# Revit family: RN 90044 Optifitt-Serra-Nippel doppio
name_source: partatom
category: Rohrformteile
units: mm (PartAtom-declared; Revit-internal decimal feet)

## family parameters
Arbeitsebenenbasiert = Nein
Beim Laden mit Abzugskörper schneiden = Nein
Bemaßung runder Anschluss = Durchmesser verwenden
Gemeinsam genutzt = Nein
Immer vertikal = Ja
Teiletyp = Nicht definiert

## types (5) — shared parameters
1.010.00.2 Blattnummer der Richtlinie = 29
1.010.00.3 Ausgabedatum (Monat) der Richtlinie = 201308
1.010.00.4 Herstellername = R. Nussbaum AG
1.010.00.5 Revisionsdatum der Datei = 20190521
1.010.00.6 Webadresse des Herstellers = http://www.nussbaum.ch
1.100.00.4 Produktbezeichnung = Versorgung
1.110.00.2 Index = 3
1.110.00.4 Produktbezeichnung = Optifitt-Serra
1.960/3L.00.8 Link (URL) = https://www.nussbaum.ch
29.700.00.4 Produktname = Optifitt-Serra-Doppelnippel, für flachdichtende Verschraubungen
29.700.00.5 Produktkennung = 2
29.700.00.6 Querschnittsform = 1
29.700.00.7 Nennweitensystem = DN
29.700.00.8 Nenndrucksystem = PN
29.710.02.4 Nenndruck = 16
29.710.02.5 max. zul. Überdruck [hPa] = 1600
29.710.02.7 max. zul. Dauer-Betriebsdruck [hPa] = 1600
29.710.02.9 max. zul. Dauer-Betriebstemperatur [°C] = 90
Connector Visibility = Nein
EnclosingSpace Visibility = Nein
Hersteller = R. Nussbaum AG
R. Nussbaum AG 90044.04 de Visibility = Nein
R. Nussbaum AG 90044.06 de Visibility = Nein
URL = https://www.nussbaum.ch

## per-type parameters (varying)
| type | 1.800.00.3 TGA-Nummer | 1.800.00.4 Kommentarfeld | 1.810.00.3 Hersteller-Bestellnummer | 1.810.00.4 DATANORM-Nummer | 1.810.00.6 GTIN-Nummer | 29.710.02.10 Formstück-Gewicht [kg] | 29.710.02.3 Benennung | CONNECTOR0_DIAMETER_dX_0r | CONNECTOR0_dX_01 | CONNECTOR0_ref_dX | CONNECTOR1_DIAMETER_dX_0r | CONNECTOR1_dX_00 | CONNECTOR1_dX_01 | CONNECTOR1_ref_dX | CONNECTOR1_ref_dX2 | Modell | R. Nussbaum AG 90044.03 de Visibility | R. Nussbaum AG 90044.05 de Visibility | R. Nussbaum AG 90044.07 de Visibility | R. Nussbaum AG 90044.08 de Visibility | R. Nussbaum AG 90044.09 de Visibility | Typenkommentare |
| DN=50 | 01900300000000000000000000000000000000000000000024000000000000000007 | 90044.09, Optifitt-Serra-Doppelnippel, für flachdichtende Verschraubungen, DN=50, L=58 | 90044.09 | 90044.09 | 7612945742094 | 0.814 | Optifitt-Serra-Doppelnippel, für flachdichtende Verschraubungen, DN=50, L=58 | 50 mm | 24 mm | 24 mm | 50 mm | 34 mm | 58 mm | 34 mm | 58 mm | 90044.09 | Nein | Nein | Nein | Nein | Ja | Optifitt-Serra-Nippel doppio  DN=50 |
| DN=40 | 01900300000000000000000000000000000000000000000024000000000000000006 | 90044.08, Optifitt-Serra-Doppelnippel, für flachdichtende Verschraubungen, DN=40, L=42 | 90044.08 | 90044.08 | 7612945742025 | 0.339 | Optifitt-Serra-Doppelnippel, für flachdichtende Verschraubungen, DN=40, L=42 | 40 mm | 19 mm | 19 mm | 40 mm | 23 mm  [stored 0.0754593 ft] | 42 mm  [stored 0.137795 ft] | 23 mm  [stored 0.0754593 ft] | 42 mm  [stored 0.137795 ft] | 90044.08 | Nein | Nein | Nein | Ja | Nein | Optifitt-Serra-Nippel doppio  DN=40 |
| DN=32 | 01900300000000000000000000000000000000000000000024000000000000000005 | 90044.07, Optifitt-Serra-Doppelnippel, für flachdichtende Verschraubungen, DN=32, L=42 | 90044.07 | 90044.07 | 7612945742018 | 0.3 | Optifitt-Serra-Doppelnippel, für flachdichtende Verschraubungen, DN=32, L=42 | 32 mm | 19 mm | 19 mm | 32 mm | 23 mm  [stored 0.0754593 ft] | 42 mm  [stored 0.137795 ft] | 23 mm  [stored 0.0754593 ft] | 42 mm  [stored 0.137795 ft] | 90044.07 | Nein | Nein | Ja | Nein | Nein | Optifitt-Serra-Nippel doppio  DN=32 |
| DN=20 | 01900300000000000000000000000000000000000000000024000000000000000003 | 90044.05, Optifitt-Serra-Doppelnippel, für flachdichtende Verschraubungen, DN=20, L=33 | 90044.05 | 90044.05 | 7612945741998 | 0.095 | Optifitt-Serra-Doppelnippel, für flachdichtende Verschraubungen, DN=20, L=33 | 20 mm | 15 mm  [stored 0.0492126 ft] | 15 mm  [stored 0.0492126 ft] | 20 mm | 18 mm  [stored 0.0590551 ft] | 33 mm  [stored 0.108268 ft] | 18 mm  [stored 0.0590551 ft] | 33 mm  [stored 0.108268 ft] | 90044.05 | Nein | Ja | Nein | Nein | Nein | Optifitt-Serra-Nippel doppio  DN=20 |
| DN=10 | 01900300000000000000000000000000000000000000000024000000000000000001 | 90044.03, Optifitt-Serra-Doppelnippel, für flachdichtende Verschraubungen, DN=10, L=26 | 90044.03 | 90044.03 | 7612945741974 | 0.044 | Optifitt-Serra-Doppelnippel, für flachdichtende Verschraubungen, DN=10, L=26 | 10 mm  [stored 0.0328084 ft] | 10 mm  [stored 0.0328084 ft] | 10 mm  [stored 0.0328084 ft] | 10 mm  [stored 0.0328084 ft] | 16 mm | 26 mm | 16 mm | 26 mm | 90044.03 | Ja | Nein | Nein | Nein | Nein | Optifitt-Serra-Nippel doppio  DN=10 |

note: [stored X ft] marks values corroborated as IEEE doubles in the binary element streams (Revit-internal decimal feet)

## geometry (parser evidence)
native form markers: Sweep x2
no freeform markers — native parametric forms only
